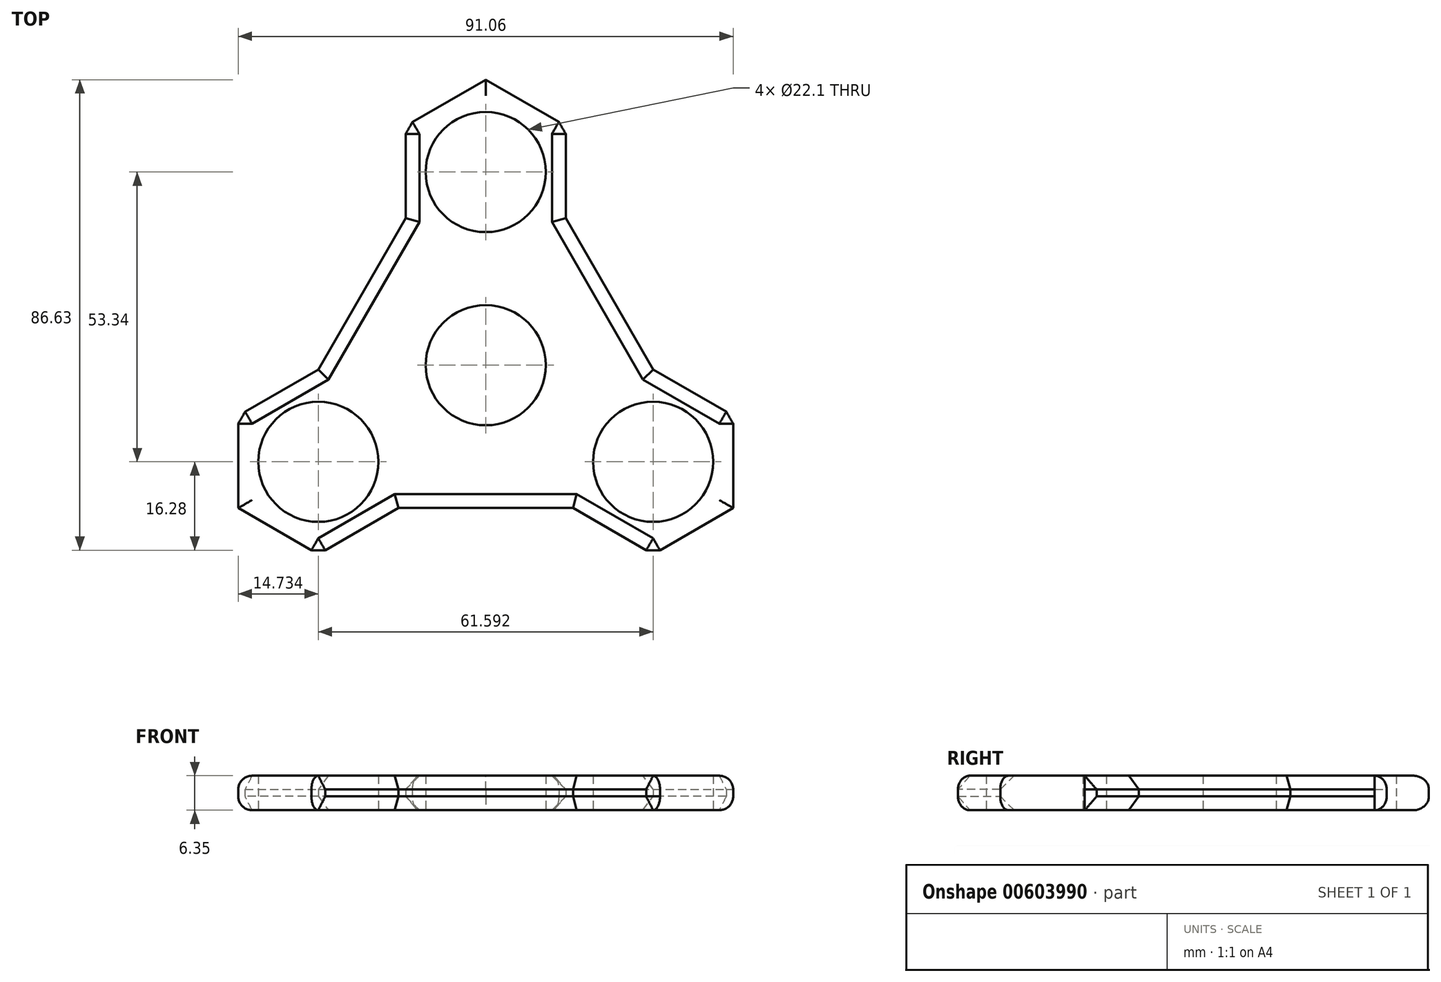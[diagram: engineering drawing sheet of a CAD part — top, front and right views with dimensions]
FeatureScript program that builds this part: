
annotation { "Feature Type Name" : "Feature", "Feature Type Description" : "" }
export const myFeature = defineFeature(function(context is Context, id is Id, definition is map)
    precondition{}
    {
        {
            var Q0;
            Q0=qCreatedBy(makeId("Top.planeOp"),FACE);
            var sketch = newSketch(context, id + "F0", { "sketchPlane" : qUnion([Q0])});
            skCircle(sketch, "E0", {"center": v(0, 0) * mm, "radius": 11.05 * mm});
            skCircle(sketch, "E1", {"center": v(0, 0) * mm, "radius": 13.97 * mm});
            skLineSegment(sketch, "E2", {"start": v(0, 0) * mm, "end": v(0, 35.56) * mm});
            skCircle(sketch, "E3", {"center": v(0, 35.56) * mm, "radius": 11.05 * mm});
            skLineSegment(sketch, "E4.0", {"start": v(14.73, 44.06) * mm, "end": v(14.73, 27.06) * mm});
            skLineSegment(sketch, "E4.1", {"start": v(14.73, 27.06) * mm, "end": v(0, 18.55) * mm});
            skLineSegment(sketch, "E4.2", {"start": v(0, 18.55) * mm, "end": v(-14.73, 27.06) * mm});
            skLineSegment(sketch, "E4.3", {"start": v(-14.73, 27.06) * mm, "end": v(-14.73, 44.06) * mm});
            skLineSegment(sketch, "E4.4", {"start": v(-14.73, 44.06) * mm, "end": v(0, 52.57) * mm});
            skLineSegment(sketch, "E4.5", {"start": v(0, 52.57) * mm, "end": v(14.73, 44.06) * mm});
            skLineSegment(sketch, "E5.1.0", {"start": v(-45.53, -26.28) * mm, "end": v(-45.53, -9.28) * mm});
            skLineSegment(sketch, "E5.1.1", {"start": v(-45.53, -9.28) * mm, "end": v(-30.8, -0.77) * mm});
            skLineSegment(sketch, "E5.1.2", {"start": v(-30.8, -34.79) * mm, "end": v(-45.53, -26.28) * mm});
            skLineSegment(sketch, "E5.1.3", {"start": v(-16.07, -26.28) * mm, "end": v(-30.8, -34.79) * mm});
            skCircle(sketch, "E5.1.4", {"center": v(-30.8, -17.78) * mm, "radius": 11.05 * mm});
            skLineSegment(sketch, "E5.1.5", {"start": v(-16.07, -9.28) * mm, "end": v(-16.07, -26.28) * mm});
            skLineSegment(sketch, "E5.1.6", {"start": v(-30.8, -0.77) * mm, "end": v(-16.07, -9.28) * mm});
            skLineSegment(sketch, "E5.2.0", {"start": v(45.53, -26.28) * mm, "end": v(30.8, -34.79) * mm});
            skLineSegment(sketch, "E5.2.1", {"start": v(30.8, -34.79) * mm, "end": v(16.07, -26.28) * mm});
            skLineSegment(sketch, "E5.2.2", {"start": v(45.53, -9.28) * mm, "end": v(45.53, -26.28) * mm});
            skLineSegment(sketch, "E5.2.3", {"start": v(30.8, -0.77) * mm, "end": v(45.53, -9.28) * mm});
            skCircle(sketch, "E5.2.4", {"center": v(30.8, -17.78) * mm, "radius": 11.05 * mm});
            skLineSegment(sketch, "E5.2.5", {"start": v(16.07, -9.28) * mm, "end": v(30.8, -0.77) * mm});
            skLineSegment(sketch, "E5.2.6", {"start": v(16.07, -26.28) * mm, "end": v(16.07, -9.28) * mm});
            skLineSegment(sketch, "E6", {"start": v(-14.73, 27.06) * mm, "end": v(-30.8, -0.77) * mm});
            skLineSegment(sketch, "E7", {"start": v(14.73, 27.06) * mm, "end": v(30.8, -0.77) * mm});
            skLineSegment(sketch, "E8", {"start": v(16.07, -26.28) * mm, "end": v(-16.07, -26.28) * mm});
            skSolve(sketch);
        }
        {
            var Q0;
            Q0=makeQuery(id+"F0.imprint","IMPRINT",FACE,{"disambiguationData":[TD([[makeQuery(id+"F0.imprint","IMPRINT",EDGE,{"derivedFrom":sQuery(id+"F0.wireOp",EDGE,"E3")}),-1.0]])]});
            var Q1;
            Q1=makeQuery(id+"F0.imprint","IMPRINT",FACE,{"disambiguationData":[TD([[makeQuery(id+"F0.imprint","IMPRINT",EDGE,{"derivedFrom":sQuery(id+"F0.wireOp",EDGE,"E5.1.0")}),-1.0]])]});
            var Q2;
            Q2=makeQuery(id+"F0.imprint","IMPRINT",FACE,{"disambiguationData":[TD([[makeQuery(id+"F0.imprint","IMPRINT",EDGE,{"derivedFrom":sQuery(id+"F0.wireOp",EDGE,"E5.2.0")}),-1.0]])]});
            var Q3;
            Q3=makeQuery(id+"F0.imprint","IMPRINT",FACE,{"disambiguationData":[TD([[makeQuery(id+"F0.imprint","IMPRINT",EDGE,{"derivedFrom":sQuery(id+"F0.wireOp",EDGE,"E1")}),-1.0]])]});
            extrude(context, id + "F1", {"entities" : qUnion([Q0, Q1, Q2, Q3]), "depth" : 6.35 * mm, "offsetDistance" : 25.4 * mm});
        }
        {
            var Q0;
            Q0=makeQuery(id+"F1.opExtrude","CAP_EDGE",EDGE,{"disambiguationData":[OSD([sQuery(id+"F0.wireOp",EDGE,"E5.1.2")])],"isStart":false});
            var Q1;
            Q1=makeQuery(id+"F1.opExtrude","CAP_EDGE",EDGE,{"disambiguationData":[OSD([sQuery(id+"F0.wireOp",EDGE,"E5.1.0")])],"isStart":false});
            var Q2;
            Q2=makeQuery(id+"F1.opExtrude","CAP_EDGE",EDGE,{"disambiguationData":[OSD([sQuery(id+"F0.wireOp",EDGE,"E5.2.0")])],"isStart":false});
            var Q3;
            Q3=makeQuery(id+"F1.opExtrude","CAP_EDGE",EDGE,{"disambiguationData":[OSD([sQuery(id+"F0.wireOp",EDGE,"E5.2.2")])],"isStart":false});
            var Q4;
            Q4=makeQuery(id+"F1.opExtrude","CAP_EDGE",EDGE,{"disambiguationData":[OSD([sQuery(id+"F0.wireOp",EDGE,"E4.5")])],"isStart":false});
            var Q5;
            Q5=makeQuery(id+"F1.opExtrude","CAP_EDGE",EDGE,{"disambiguationData":[OSD([sQuery(id+"F0.wireOp",EDGE,"E4.4")])],"isStart":false});
            var Q6;
            Q6=makeQuery(id+"F1.opExtrude","CAP_EDGE",EDGE,{"disambiguationData":[OSD([sQuery(id+"F0.wireOp",EDGE,"E5.1.2")])],"isStart":true});
            var Q7;
            Q7=makeQuery(id+"F1.opExtrude","CAP_EDGE",EDGE,{"disambiguationData":[OSD([sQuery(id+"F0.wireOp",EDGE,"E5.1.0")])],"isStart":true});
            var Q8;
            Q8=makeQuery(id+"F1.opExtrude","CAP_EDGE",EDGE,{"disambiguationData":[OSD([sQuery(id+"F0.wireOp",EDGE,"E5.2.0")])],"isStart":true});
            var Q9;
            Q9=makeQuery(id+"F1.opExtrude","CAP_EDGE",EDGE,{"disambiguationData":[OSD([sQuery(id+"F0.wireOp",EDGE,"E5.2.2")])],"isStart":true});
            var Q10;
            Q10=makeQuery(id+"F1.opExtrude","CAP_EDGE",EDGE,{"disambiguationData":[OSD([sQuery(id+"F0.wireOp",EDGE,"E4.5")])],"isStart":true});
            var Q11;
            Q11=makeQuery(id+"F1.opExtrude","CAP_EDGE",EDGE,{"disambiguationData":[OSD([sQuery(id+"F0.wireOp",EDGE,"E4.4")])],"isStart":true});
            fillet(context, id + "F2", {"entities" : qUnion([Q0, Q1, Q2, Q3, Q4, Q5, Q6, Q7, Q8, Q9, Q10, Q11]), "radius" : 2.54 * mm, "tangentPropagation" : true, "allowEdgeOverflow" : false});
        }
        {
            var Q0;
            Q0=makeQuery(id+"F1.opExtrude","CAP_EDGE",EDGE,{"disambiguationData":[OSD([sQuery(id+"F0.wireOp",EDGE,"E6")])],"isStart":false});
            var Q1;
            Q1=makeQuery(id+"F1.opExtrude","CAP_EDGE",EDGE,{"disambiguationData":[OSD([sQuery(id+"F0.wireOp",EDGE,"E7")])],"isStart":false});
            var Q2;
            Q2=makeQuery(id+"F1.opExtrude","CAP_EDGE",EDGE,{"disambiguationData":[OSD([sQuery(id+"F0.wireOp",EDGE,"E8")])],"isStart":false});
            var Q3;
            Q3=makeQuery(id+"F1.opExtrude","CAP_EDGE",EDGE,{"disambiguationData":[OSD([sQuery(id+"F0.wireOp",EDGE,"E8")])],"isStart":true});
            var Q4;
            Q4=makeQuery(id+"F1.opExtrude","CAP_EDGE",EDGE,{"disambiguationData":[OSD([sQuery(id+"F0.wireOp",EDGE,"E7")])],"isStart":true});
            var Q5;
            Q5=makeQuery(id+"F1.opExtrude","CAP_EDGE",EDGE,{"disambiguationData":[OSD([sQuery(id+"F0.wireOp",EDGE,"E6")])],"isStart":true});
            var Q6;
            Q6=makeQuery(id+"F1.opExtrude","CAP_EDGE",EDGE,{"disambiguationData":[OSD([sQuery(id+"F0.wireOp",EDGE,"E5.1.3")])],"isStart":false});
            var Q7;
            Q7=makeQuery(id+"F1.opExtrude","CAP_EDGE",EDGE,{"disambiguationData":[OSD([sQuery(id+"F0.wireOp",EDGE,"E5.2.1")])],"isStart":false});
            var Q8;
            Q8=makeQuery(id+"F1.opExtrude","CAP_EDGE",EDGE,{"disambiguationData":[OSD([sQuery(id+"F0.wireOp",EDGE,"E5.2.3")])],"isStart":false});
            var Q9;
            Q9=makeQuery(id+"F1.opExtrude","CAP_EDGE",EDGE,{"disambiguationData":[OSD([sQuery(id+"F0.wireOp",EDGE,"E5.1.1")])],"isStart":false});
            var Q10;
            Q10=makeQuery(id+"F1.opExtrude","CAP_EDGE",EDGE,{"disambiguationData":[OSD([sQuery(id+"F0.wireOp",EDGE,"E4.3")])],"isStart":false});
            var Q11;
            Q11=makeQuery(id+"F1.opExtrude","CAP_EDGE",EDGE,{"disambiguationData":[OSD([sQuery(id+"F0.wireOp",EDGE,"E4.0")])],"isStart":false});
            var Q12;
            Q12=makeQuery(id+"F1.opExtrude","CAP_EDGE",EDGE,{"disambiguationData":[OSD([sQuery(id+"F0.wireOp",EDGE,"E5.1.3")])],"isStart":true});
            var Q13;
            Q13=makeQuery(id+"F1.opExtrude","CAP_EDGE",EDGE,{"disambiguationData":[OSD([sQuery(id+"F0.wireOp",EDGE,"E5.2.1")])],"isStart":true});
            var Q14;
            Q14=makeQuery(id+"F1.opExtrude","CAP_EDGE",EDGE,{"disambiguationData":[OSD([sQuery(id+"F0.wireOp",EDGE,"E5.2.3")])],"isStart":true});
            var Q15;
            Q15=makeQuery(id+"F1.opExtrude","CAP_EDGE",EDGE,{"disambiguationData":[OSD([sQuery(id+"F0.wireOp",EDGE,"E5.1.1")])],"isStart":true});
            chamfer(context, id + "F3", {"entities" : qUnion([Q0, Q1, Q2, Q3, Q4, Q5, Q6, Q7, Q8, Q9, Q10, Q11, Q12, Q13, Q14, Q15]), "width" : 2.54 * mm, "tangentPropagation" : true});
        }
        {
            var Q0;
            Q0=makeQuery(id+"F0.imprint","IMPRINT",FACE,{"disambiguationData":[TD([[makeQuery(id+"F0.imprint","IMPRINT",EDGE,{"derivedFrom":sQuery(id+"F0.wireOp",EDGE,"E0")}),-1.0]])]});
            extrude(context, id + "F4", {"entities" : qUnion([Q0]), "operationType" : NewBodyOperationType.ADD, "depth" : 6.35 * mm, "offsetDistance" : 25.4 * mm});
        }
    });
